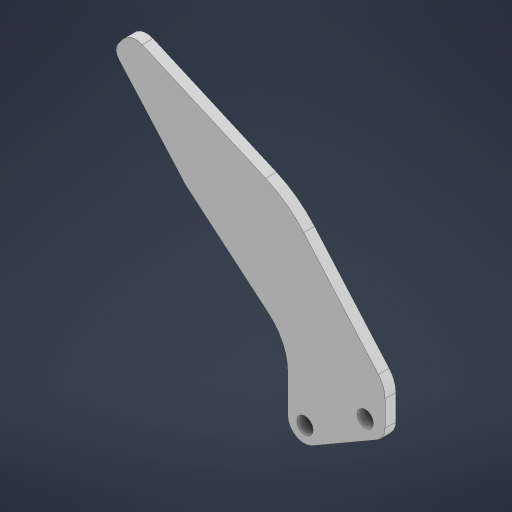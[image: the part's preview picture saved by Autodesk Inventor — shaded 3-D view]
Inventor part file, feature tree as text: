
AUTODESK INVENTOR PART (.ipt)
format: ipt  version: 2023 (Build 270158000, 158)  size: 253,440 bytes
history: native  units: mm
features: fillet x7, extrude x6, sketch x5, chamfer x2
ambient origin geometry x8: Origin, YZ Plane, XZ Plane, XY Plane, X Axis, Y Axis, Z Axis, Center Point
bodies: Solid1 (feature_tree)
feature tree (20):
  extrude  "Extrusion1"  Depth=30.0mm
  fillet  "Fillet1"  [1 undecoded]
  extrude  "Extrusion2"  Depth=3.0mm
  sketch  "Sketch3"  dims[d8=3.0mm d9=21.816616mm]
  extrude  "Extrusion3"  Depth=3.0mm
  extrude  "Extrusion4"  Depth=3.0mm
  fillet  "Fillet2"  Radius=3.0mm
  chamfer  "Chamfer1"  Distance=2.0mm
  fillet  "Fillet3"  Radius=22.68928mm
  extrude  "Extrusion5"  Depth=2.0mm
  fillet  "Fillet4"  [1 undecoded]
  extrude  "Extrusion6"  Depth=2.0mm TaperAngle=0.0deg
  fillet  "Fillet5"  Radius=2.0mm
  fillet  "Fillet6"  Radius=10.0mm
  chamfer  "Chamfer2"  Distance=5.0mm Angle=45.0deg
  fillet  "Fillet7"  Radius=20.0mm
  sketch  "Sketch1"  dims[d0=18.0mm d1=30.0mm d2=30.0deg]
  sketch  "Sketch2"  dims[d3=2.0mm d4=0.0mm d5=3.0mm]
  sketch  "Sketch4"  dims[d10=6.5mm d11=13.0mm d12=3.0mm]
  sketch  "Sketch5"  dims[d13=3.0mm d14=2.0mm d15=0.0mm d16=22.68928mm d17=50.0mm d18=90.0deg d19=2.0mm d20=0.0mm d21=2.0mm d22=0.0mm d23=10.0mm d24=5.0mm d25=40.0mm d26=45.0deg d27=20.0mm d28=2.0mm d29=0.0mm d30=5.0mm d31=2.0mm d32=0.0mm d33=20.0mm d34=3.0mm d35=20.0mm d36=3.0mm d37=45.0deg d38=2.0mm]
note: 2 required parameter values undecoded (feature->parameter linkage not recoverable at this tier; creation-order binding heuristic only, values carry confidence <= 0.55)
